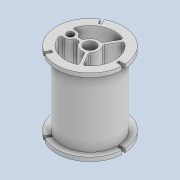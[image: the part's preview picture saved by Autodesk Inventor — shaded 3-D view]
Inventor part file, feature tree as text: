
AUTODESK INVENTOR PART (.ipt)
format: ipt  version: 2020 (Build 240168000, 168)  size: 309,760 bytes
history: native  units: mm
features: extrude x5, sketch x5, projected_geometry x4, fillet x2, pattern_circular x1
ambient origin geometry x8: Origin, YZ Plane, XZ Plane, XY Plane, X Axis, Y Axis, Z Axis, Center Point
bodies: Solid1 (feature_tree)
feature tree (17):
  extrude  "Extrusion1"  Depth=3.0mm
  extrude  "Extrusion2"  Depth=0.7mm
  extrude  "Extrusion3"  Depth=0.7mm
  extrude  "Extrusion4"  Depth=5.0mm
  extrude  "Extrusion5"  Depth=19.5mm TaperAngle=0.0deg
  pattern_circular  "Circular Pattern1"  [2 undecoded]
  fillet  "Fillet1"  Radius=19.5mm
  fillet  "Fillet2"  Radius=1.5mm
  sketch  "Sketch1"  dims[d0=14.0mm d1=3.0mm]
  sketch  "Sketch2"  dims[d2=0.7mm d3=0.7mm]
  projected_geometry  "Projected Loop1"
  sketch  "Sketch3"  dims[d4=3.5mm d5=0.7mm]
  projected_geometry  "Projected Loop2"
  sketch  "Sketch4"  dims[d6=30.0mm d8=360.0deg d10=5.0mm]
  projected_geometry  "Projected Loop3"
  sketch  "Sketch5"  dims[d11=3.0mm d12=19.5mm d13=0.0mm d14=1.8mm d15=19.5mm d16=0.0mm d17=1.5mm d18=1.0mm d19=0.0mm d20=1.0mm d21=0.0mm d22=60.0deg d23=3.0mm d24=0.7mm d25=20.0mm d26=0.0mm d27=30.0mm d28=360.0deg d30=0.2mm d31=0.5mm]
  projected_geometry  "Projected Loop4"
note: 2 required parameter values undecoded (feature->parameter linkage not recoverable at this tier; creation-order binding heuristic only, values carry confidence <= 0.55)
